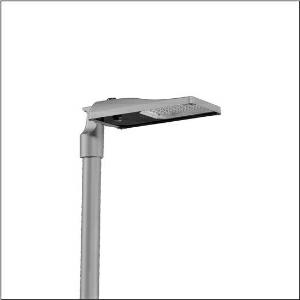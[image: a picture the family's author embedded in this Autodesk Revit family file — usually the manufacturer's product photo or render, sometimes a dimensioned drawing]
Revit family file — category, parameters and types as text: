
# Revit family: streetlight_sl_31_mini___p1_0a_5xh6a31t08ha_087d
name_source: partatom
category: Lighting Fixtures
units: mm (PartAtom-declared; Revit-internal decimal feet)

## family parameters
Cut with Voids When Loaded = No
Host = Face
Light Source = No
Part Type = Normal
Room Calculation Point = No
Round Connector Dimension = Use Diameter
Shared = No

## types (1)
- --- (1 x LED, 8970 lm, 68.3 W, 3000K)
    Apparent Load = 68 VA
    CIE Flux Codes = 23 55 94 100 100
    Color Rendering = 70
    Color Temperature = 3000K
    Default Elevation = 1800 mm
    Description = Streetlight SL 31 mini D4i, Desk-Remote mast luminaire for post-top, side-entry; light control with lens of PMMA; light distribution: P1.0a, direct asymmetric distribution, for standard-compliant lighting for roads and squares; LED: luminous flux: 8.970lm, light colour: 730, colour temperature: 3000K; luminous efficacy: 131,3lm/W; control: pre-setting: logarithmic dimming characteristic, flexible luminous flux parameterisation, time-dependent luminous flux control, constant luminous flux control, power reduction, intelligent temperature release in ECG and LED module, overheat protection; luminaire housing, of diecast aluminium, Siteco® metallic grey (DB 702S), corrosivity category C5 high according to DIN EN ISO 12944; cover of toughened safety glass, transparent, opened without tools; mast flange of diecast aluminium, Siteco® metallic grey (DB 702S), spigot size: 76/60mm, mast flange included unmounted; with cable H07RN-F 2x 1.5mm², cable length: 8,5m, connection cable pre-assembled; mains connection: 220..240V, AC, 50/60Hz; power consumption (at start of service life): 68,3W / (at end of service life): 74,5W / (with reduced operation 50%): 29,5W; protection rating (complete): IP66; insulation class (complete): insulation class II (safety insulation); impact resistance: IK09; certification: CE, ENEC, ENEC+, VDE, UKCA, ZD4i; permissible operating ambient temperature for outdoor applications: -40..+50°C; packaging unit: 1 piece

Light Distribution: P1.0a
    Height = 76 mm
    Lamp = 1 x LED
    Lamp Light Flux = 8970 lm
    Lamp Power = 68.3 W
    Lamp count = 1
    Length = 547 mm
    Luminous efficacy = 131 lm/W
    Manufacturer = Siteco
    ModVariant = No
    Model = 5XH6A31T08HA
    Number of Poles = 1
    OnlyDefault = Yes
    Power Factor = 1
    Product Name = Streetlight SL 31 mini | P1.0a
    Product group = mast luminaire | pylon top
    ProductGroupID = 6100
    Protection Class = Protection class II
    Protection Degree = IP 66
    RLX_Detail_Level = 1
    RLX_Emergency_Light_Flux = 0 lm
    RLX_Emergency_Type = 0
    RLX_Emergency_Type_DB = No
    RlxData = <blob elided: 24073 chars, md5=84df6b98>
    Socket = socket
    Standby Power = 0 W
    System Light Flux = 8970 lm
    System Power = 68 W
    Type Comments = factory setting: luminous flux: 100 % | dim-lin: 254 | 692 mA
    Type Image = l_1300332.jpg
    URL = http://relux.com
    VarID = @adj_006491
    Voltage = 0 V
    Weight = 0.00 kg
    Width = 265 mm

## geometry (parser evidence)
native form markers: Blend x4, Sweep x11
no freeform markers — native parametric forms only
